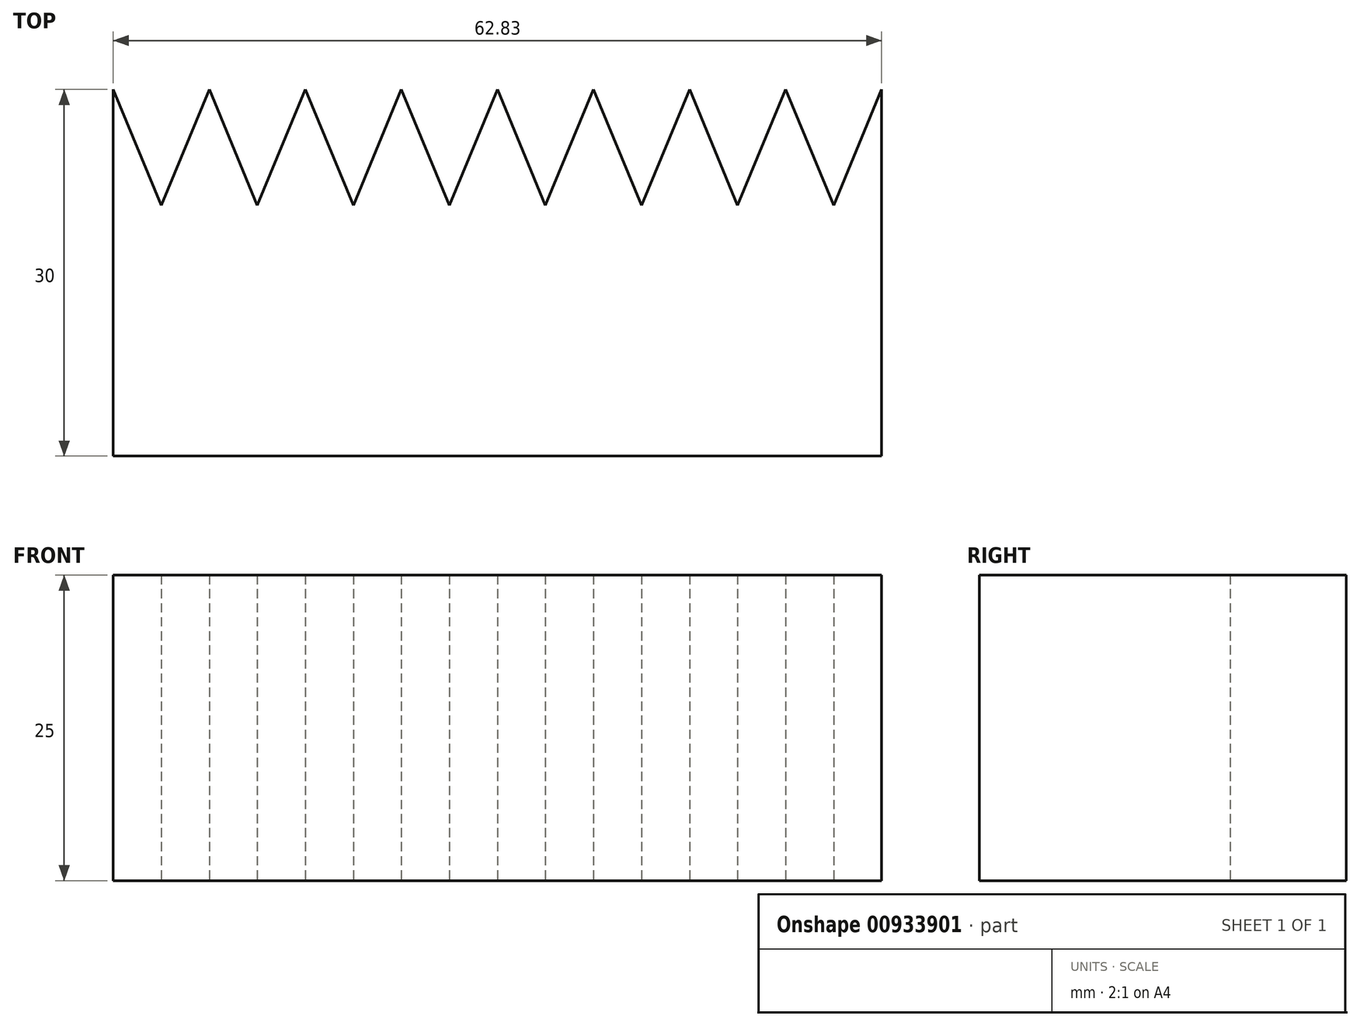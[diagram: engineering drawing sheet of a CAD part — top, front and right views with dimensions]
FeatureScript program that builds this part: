
annotation { "Feature Type Name" : "Feature", "Feature Type Description" : "" }
export const myFeature = defineFeature(function(context is Context, id is Id, definition is map)
    precondition{}
    {
        {
            var Q0;
            Q0=qCreatedBy(makeId("Top.planeOp"),FACE);
            var sketch = newSketch(context, id + "F0", { "sketchPlane" : qUnion([Q0])});
            skLineSegment(sketch, "E0", {"start": v(0, 0) * mm, "end": v(3.93, -9.48) * mm});
            skLineSegment(sketch, "E1", {"start": v(3.93, -9.48) * mm, "end": v(7.85, 0) * mm});
            skLineSegment(sketch, "E2", {"start": v(0, 0) * mm, "end": v(0, -30) * mm});
            skLineSegment(sketch, "E3.1.0.0", {"start": v(7.85, 0) * mm, "end": v(11.78, -9.48) * mm});
            skLineSegment(sketch, "E3.1.0.1", {"start": v(11.78, -9.48) * mm, "end": v(15.7, 0) * mm});
            skLineSegment(sketch, "E3.2.0.0", {"start": v(15.7, 0) * mm, "end": v(19.63, -9.48) * mm});
            skLineSegment(sketch, "E3.2.0.1", {"start": v(19.63, -9.48) * mm, "end": v(23.56, 0) * mm});
            skLineSegment(sketch, "E3.3.0.0", {"start": v(23.56, 0) * mm, "end": v(27.49, -9.48) * mm});
            skLineSegment(sketch, "E3.3.0.1", {"start": v(27.49, -9.48) * mm, "end": v(31.42, 0) * mm});
            skLineSegment(sketch, "E3.4.0.0", {"start": v(31.42, 0) * mm, "end": v(35.34, -9.48) * mm});
            skLineSegment(sketch, "E3.4.0.1", {"start": v(35.34, -9.48) * mm, "end": v(39.27, 0) * mm});
            skLineSegment(sketch, "E3.5.0.0", {"start": v(39.27, 0) * mm, "end": v(43.2, -9.48) * mm});
            skLineSegment(sketch, "E3.5.0.1", {"start": v(43.2, -9.48) * mm, "end": v(47.12, 0) * mm});
            skLineSegment(sketch, "E3.6.0.0", {"start": v(47.12, 0) * mm, "end": v(51.05, -9.48) * mm});
            skLineSegment(sketch, "E3.6.0.1", {"start": v(51.05, -9.48) * mm, "end": v(54.98, 0) * mm});
            skLineSegment(sketch, "E3.7.0.0", {"start": v(54.98, 0) * mm, "end": v(58.9, -9.48) * mm});
            skLineSegment(sketch, "E3.7.0.1", {"start": v(58.9, -9.48) * mm, "end": v(62.83, 0) * mm});
            skLineSegment(sketch, "E3.direction1", {"start": v(3.93, -9.48) * mm, "end": v(11.78, -9.48) * mm, "construction": true});
            skLineSegment(sketch, "E4", {"start": v(0, -30) * mm, "end": v(62.83, -30) * mm});
            skLineSegment(sketch, "E5", {"start": v(62.83, -30) * mm, "end": v(62.83, 0) * mm});
            skSolve(sketch);
        }
        {
            var Q0;
            Q0=makeQuery(id+"F0.imprint","IMPRINT",FACE,{"disambiguationData":[TD([[makeQuery(id+"F0.imprint","IMPRINT",EDGE,{"derivedFrom":sQuery(id+"F0.wireOp",EDGE,"E0")}),-1.0]])]});
            extrude(context, id + "F1", {"entities" : qUnion([Q0]), "depth" : 25 * mm, "offsetDistance" : 25 * mm});
        }
    });
